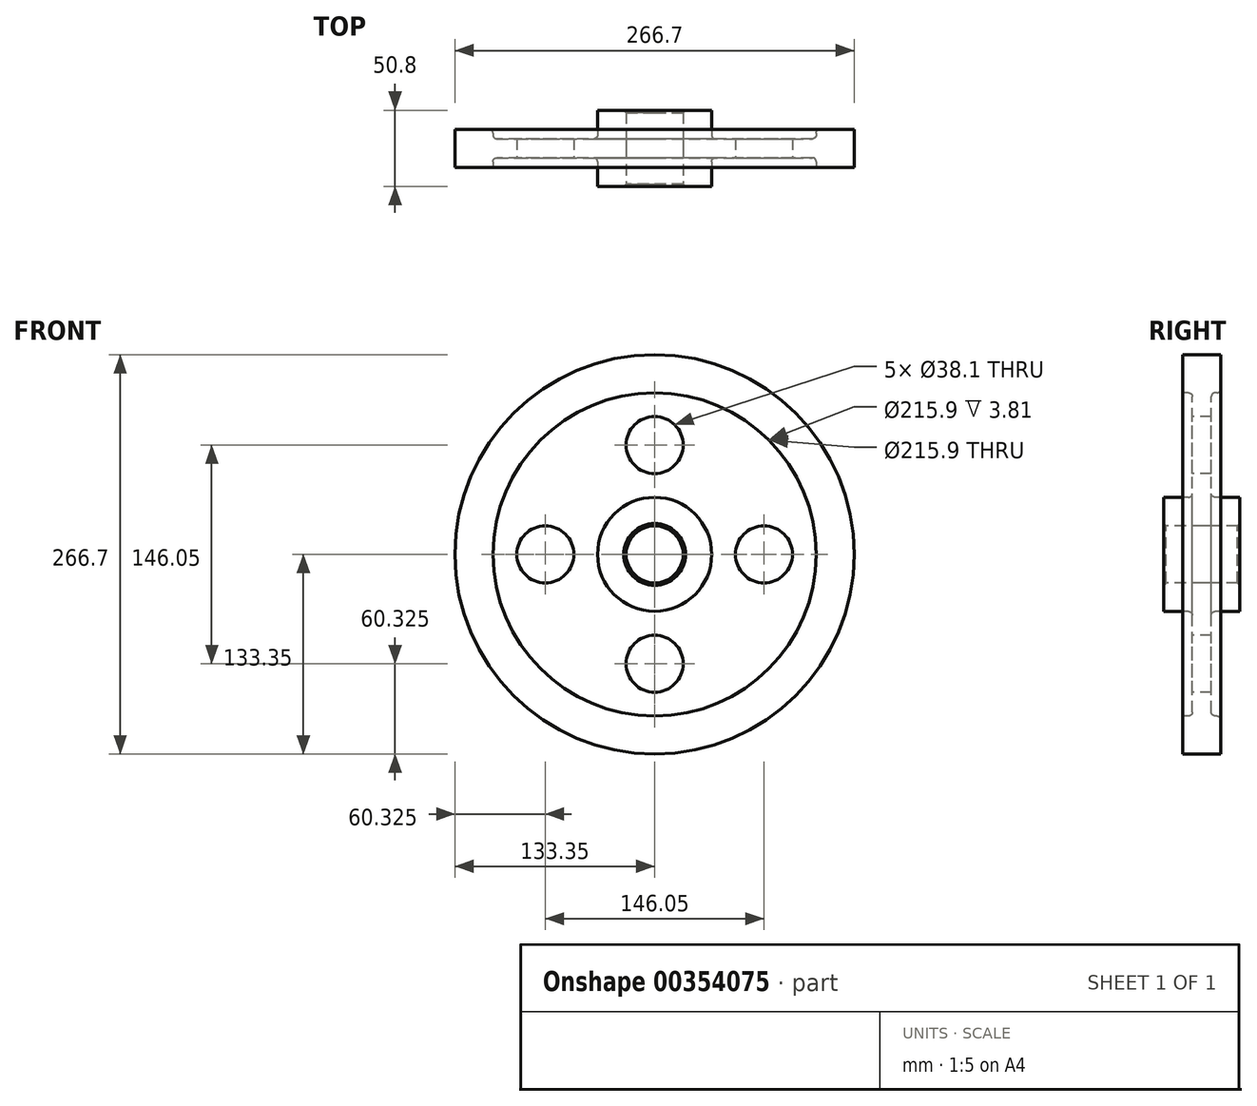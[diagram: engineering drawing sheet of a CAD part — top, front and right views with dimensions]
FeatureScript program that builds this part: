
annotation { "Feature Type Name" : "Feature", "Feature Type Description" : "" }
export const myFeature = defineFeature(function(context is Context, id is Id, definition is map)
    precondition{}
    {
        {
            var Q0;
            Q0=qCreatedBy(makeId("Right.planeOp"),FACE);
            var sketch = newSketch(context, id + "F0", { "sketchPlane" : qUnion([Q0])});
            skLineSegment(sketch, "E0", {"start": v(0, 0) * mm, "end": v(94.54, 0) * mm, "construction": true});
            skLineSegment(sketch, "E1.0", {"start": v(6.35, 19.05) * mm, "end": v(25.4, 19.05) * mm});
            skLineSegment(sketch, "E2.0", {"start": v(6.35, 107.95) * mm, "end": v(12.7, 107.95) * mm});
            skLineSegment(sketch, "E3.0", {"start": v(0, 133.35) * mm, "end": v(12.7, 133.35) * mm});
            skLineSegment(sketch, "E4", {"start": v(0, 0) * mm, "end": v(0, 133.35) * mm, "construction": true});
            skLineSegment(sketch, "E5.1", {"start": v(6.35, 38.1) * mm, "end": v(6.35, 107.95) * mm});
            skLineSegment(sketch, "E6.0", {"start": v(12.7, 107.95) * mm, "end": v(12.7, 133.35) * mm});
            skLineSegment(sketch, "E7.0", {"start": v(6.35, 38.1) * mm, "end": v(25.4, 38.1) * mm});
            skLineSegment(sketch, "E8", {"start": v(25.4, 19.05) * mm, "end": v(25.4, 38.1) * mm});
            skLineSegment(sketch, "E9", {"start": v(6.35, 19.05) * mm, "end": v(0, 19.05) * mm});
            skLineSegment(sketch, "E10.MirrorCS", {"start": v(0, 133.35) * mm, "end": v(-12.7, 133.35) * mm});
            skLineSegment(sketch, "E11.MirrorCS", {"start": v(-12.7, 107.95) * mm, "end": v(-12.7, 133.35) * mm});
            skLineSegment(sketch, "E12.MirrorCS", {"start": v(-6.35, 38.1) * mm, "end": v(-6.35, 107.95) * mm});
            skLineSegment(sketch, "E13.MirrorCS", {"start": v(-6.35, 38.1) * mm, "end": v(-25.4, 38.1) * mm});
            skLineSegment(sketch, "E14.MirrorCS", {"start": v(-25.4, 19.05) * mm, "end": v(-25.4, 38.1) * mm});
            skLineSegment(sketch, "E15.MirrorCS", {"start": v(-6.35, 19.05) * mm, "end": v(-25.4, 19.05) * mm});
            skLineSegment(sketch, "E16.MirrorCS", {"start": v(-6.35, 19.05) * mm, "end": v(0, 19.05) * mm});
            skLineSegment(sketch, "E17.MirrorCS", {"start": v(0, 107.95) * mm, "end": v(-12.7, 107.95) * mm});
            skLineSegment(sketch, "E18.MirrorCS", {"start": v(-6.35, 107.95) * mm, "end": v(-12.7, 107.95) * mm});
            skPoint(sketch, "E19.orphan", {"position": v(0, 107.95) * mm});
            skSolve(sketch);
        }
        {
            var Q0;
            Q0=makeQuery(id+"F0.imprint","IMPRINT",FACE,{"disambiguationData":[TD([[makeQuery(id+"F0.imprint","IMPRINT",EDGE,{"derivedFrom":sQuery(id+"F0.wireOp",EDGE,"E1.0")}),1.0]])]});
            var Q1;
            Q1=sQuery(id+"F0.wireOp",EDGE,"E0");
            revolve(context, id + "F1", {"entities" : qUnion([Q0]), "axis" : qUnion([Q1]), "revolveType" : RevolveType.FULL});
        }
        {
            var Q0;
            Q0=makeQuery(id+"F1.opRevolve","SWEPT_FACE",FACE,{"disambiguationData":[OSD([sQuery(id+"F0.wireOp",EDGE,"E12.MirrorCS")])]});
            var sketch = newSketch(context, id + "F2", { "sketchPlane" : qUnion([Q0])});
            skLineSegment(sketch, "E20", {"start": v(0, 0) * mm, "end": v(0, 73.03) * mm});
            skCircle(sketch, "E21", {"center": v(0, 73.03) * mm, "radius": 19.05 * mm});
            skCircle(sketch, "E22.1.0", {"center": v(-73.03, 0) * mm, "radius": 19.05 * mm});
            skCircle(sketch, "E22.2.0", {"center": v(0, -73.03) * mm, "radius": 19.05 * mm});
            skCircle(sketch, "E22.3.0", {"center": v(73.03, 0) * mm, "radius": 19.05 * mm});
            skPoint(sketch, "E22.center", {"position": v(0, 0) * mm});
            skSolve(sketch);
        }
        {
            var Q0;
            Q0=makeQuery(id+"F2.imprint","IMPRINT",FACE,{"disambiguationData":[TD([[makeQuery(id+"F2.imprint","IMPRINT",EDGE,{"derivedFrom":sQuery(id+"F2.wireOp",EDGE,"E22.1.0")}),1.0]])]});
            var Q1;
            Q1=makeQuery(id+"F2.imprint","IMPRINT",FACE,{"disambiguationData":[TD([[makeQuery(id+"F2.imprint","IMPRINT",EDGE,{"derivedFrom":sQuery(id+"F2.wireOp",EDGE,"E22.2.0")}),1.0]])]});
            var Q2;
            Q2=makeQuery(id+"F2.imprint","IMPRINT",FACE,{"disambiguationData":[TD([[makeQuery(id+"F2.imprint","IMPRINT",EDGE,{"derivedFrom":sQuery(id+"F2.wireOp",EDGE,"E22.3.0")}),1.0]])]});
            var Q3;
            Q3=makeQuery(id+"F2.imprint","IMPRINT",FACE,{"disambiguationData":[TD([[makeQuery(id+"F2.imprint","IMPRINT",EDGE,{"derivedFrom":sQuery(id+"F2.wireOp",EDGE,"E21")}),1.0]])]});
            extrude(context, id + "F3", {"entities" : qUnion([Q0, Q1, Q2, Q3]), "operationType" : NewBodyOperationType.REMOVE, "oppositeDirection" : true, "depth" : 25.4 * mm});
        }
        {
            var Q0;
            Q0=makeQuery(id+"F1.opRevolve","SWEPT_EDGE",EDGE,{"disambiguationData":[OSD([sQuery(id+"F0.wireOp",EDGE,"E12.MirrorCS"),sQuery(id+"F0.wireOp",EDGE,"E13.MirrorCS")])]});
            var Q1;
            Q1=makeQuery(id+"F1.opRevolve","SWEPT_EDGE",EDGE,{"disambiguationData":[OSD([sQuery(id+"F0.wireOp",EDGE,"E5.1"),sQuery(id+"F0.wireOp",EDGE,"E7.0")])]});
            var Q2;
            Q2=makeQuery(id+"F1.opRevolve","SWEPT_EDGE",EDGE,{"disambiguationData":[OSD([sQuery(id+"F0.wireOp",EDGE,"E2.0"),sQuery(id+"F0.wireOp",EDGE,"E6.0")])]});
            var Q3;
            Q3=makeQuery(id+"F1.opRevolve","SWEPT_EDGE",EDGE,{"disambiguationData":[OSD([sQuery(id+"F0.wireOp",EDGE,"E12.MirrorCS"),sQuery(id+"F0.wireOp",EDGE,"E18.MirrorCS")])]});
            fillet(context, id + "F4", {"entities" : qUnion([Q0, Q1, Q2, Q3]), "radius" : 2.54 * mm, "tangentPropagation" : true, "allowEdgeOverflow" : false});
        }
        {
            var Q0;
            {var subQ0=sQuery(id+"F0.wireOp",EDGE,"E5.1");Q0=makeQuery(id+"F4.opFillet","BLEND_EDGE",EDGE,{"blendedFrom":[makeQuery(id+"F1.opRevolve","SWEPT_EDGE",EDGE,{"disambiguationData":[OSD([subQ0,sQuery(id+"F0.wireOp",EDGE,"E7.0")])]}),makeQuery(id+"F1.opRevolve","SWEPT_FACE",FACE,{"disambiguationData":[OSD([subQ0])]})],"blendedInto":[makeQuery(id+"F1.opRevolve","SWEPT_FACE",FACE,{"disambiguationData":[OSD([subQ0])]})]});}
            var Q1;
            {var subQ0=sQuery(id+"F0.wireOp",EDGE,"E7.0");Q1=makeQuery(id+"F4.opFillet","BLEND_EDGE",EDGE,{"blendedFrom":[makeQuery(id+"F1.opRevolve","SWEPT_EDGE",EDGE,{"disambiguationData":[OSD([sQuery(id+"F0.wireOp",EDGE,"E5.1"),subQ0])]}),makeQuery(id+"F1.opRevolve","SWEPT_FACE",FACE,{"disambiguationData":[OSD([subQ0])]})],"blendedInto":[makeQuery(id+"F1.opRevolve","SWEPT_FACE",FACE,{"disambiguationData":[OSD([subQ0])]})]});}
            var Q2;
            {var subQ0=sQuery(id+"F0.wireOp",EDGE,"E6.0");Q2=makeQuery(id+"F4.opFillet","BLEND_EDGE",EDGE,{"blendedFrom":[makeQuery(id+"F1.opRevolve","SWEPT_EDGE",EDGE,{"disambiguationData":[OSD([sQuery(id+"F0.wireOp",EDGE,"E2.0"),subQ0])]}),makeQuery(id+"F1.opRevolve","SWEPT_FACE",FACE,{"disambiguationData":[OSD([subQ0])]})],"blendedInto":[makeQuery(id+"F1.opRevolve","SWEPT_FACE",FACE,{"disambiguationData":[OSD([subQ0])]})]});}
            var Q3;
            Q3=makeQuery(id+"F1.opRevolve","SWEPT_EDGE",EDGE,{"disambiguationData":[OSD([sQuery(id+"F0.wireOp",EDGE,"E2.0"),sQuery(id+"F0.wireOp",EDGE,"E5.1")])]});
            fillet(context, id + "F5", {"entities" : qUnion([Q0, Q1, Q2, Q3]), "radius" : 2.54 * mm, "tangentPropagation" : true, "allowEdgeOverflow" : false});
        }
        {
            var Q0;
            Q0=makeQuery(id+"F1.opRevolve","SWEPT_EDGE",EDGE,{"disambiguationData":[OSD([sQuery(id+"F0.wireOp",EDGE,"E14.MirrorCS"),sQuery(id+"F0.wireOp",EDGE,"E15.MirrorCS")])]});
            var Q1;
            Q1=makeQuery(id+"F1.opRevolve","SWEPT_EDGE",EDGE,{"disambiguationData":[OSD([sQuery(id+"F0.wireOp",EDGE,"E1.0"),sQuery(id+"F0.wireOp",EDGE,"E8")])]});
            chamfer(context, id + "F6", {"entities" : qUnion([Q0, Q1]), "width" : 1.59 * mm, "tangentPropagation" : true});
        }
    });
